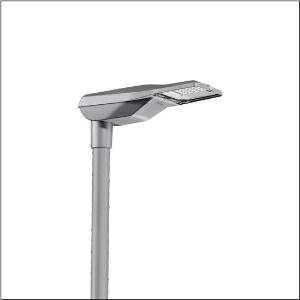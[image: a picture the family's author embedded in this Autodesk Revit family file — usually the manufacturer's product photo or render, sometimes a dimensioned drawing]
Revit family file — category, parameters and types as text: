
# Revit family: streetlight_sl_21_iq_micro___st1_5a_5xe1p41g08cb_60b9
name_source: partatom
category: Lighting Fixtures
units: mm (PartAtom-declared; Revit-internal decimal feet)

## family parameters
Cut with Voids When Loaded = No
Host = Face
Light Source = No
Part Type = Normal
Room Calculation Point = No
Round Connector Dimension = Use Diameter
Shared = No

## types (1)
- --- (1 x LED, 2930 lm, 19.4 W, 4000K)
    Apparent Load = 19 VA
    CIE Flux Codes = 22 53 95 100 100
    Color Rendering = 70
    Color Temperature = 4000K
    Default Elevation = 1800 mm
    Description = Streetlight SL 21 iQ micro, mast luminaire, primary light control with lens, of PMMA, primary optical cover: cover, of toughened safety glass, transparent, light distribution: ST1.5a, light emission: direct distribution, primary light characteristic: asymmetric, installation type: post-top, side-entry, LED, High Power LED, rated luminous flux: 2.930lm, luminous efficacy: 151lm/W, light colour: 740, colour temperature: 4000K, control: Street-Remote, Auto-Match, Temp-Guard, Lumen-Switch, Night-Set, Smart-Wire, Light-Fading, Desk-Remote (wireless, voltage-free reading and setting of iQ features in the workshop via application-optimized NFC function/RFID function), optimised constant luminous flux control (CLO 2.0), presetting dimming linear, mains connection: 220..240V, AC, 50/60Hz, start of lifetime: 19W, end of service life: 20W, reduction: 10W, luminaire housing, of diecast aluminium, powder-coated, Siteco® metallic grey (DB 702S), corrosivity category C5 mid according to DIN EN ISO 12944, please order mast flange separately, inclination adjustable: 0°, 5°, 10°, 15°, sealing non-destructively replaceable, multi-level sealing system, length: 528mm, width: 235mm, height: 110mm, mast flange for spigot size: 42mm (side-entry): 5XC10008XM4, 60/48mm (side-entry/post-top): 5XC10108XM2, 76/60mm (side-entry/post-top): 5XC10108XM1, protection rating (complete): IP66, insulation class (complete): insulation class II (safety insulation), certification: CE, ENEC, ENEC+, VDE, impact resistance: IK09, permissible operating ambient temperature for outdoor applications: -40..+50°C, standard-compliant lighting for roads and squares, packaging unit: 1 piece

Light Distribution: ST1.5a
    Height = 110 mm
    Lamp = 1 x LED
    Lamp Light Flux = 2930 lm
    Lamp Power = 19.4 W
    Lamp count = 1
    Length = 528 mm
    Luminous efficacy = 151 lm/W
    Manufacturer = Siteco
    ModVariant = No
    Model = 5XE1P41G08CB
    Number of Poles = 1
    OnlyDefault = Yes
    Power Factor = 1
    Product Name = Streetlight SL 21 iQ micro | ST1.5a
    Product group = mast luminaire | pylon top
    ProductGroupID = 6100
    Protection Class = Protection class II
    Protection Degree = IP 66
    RLX_Detail_Level = 1
    RLX_Emergency_Light_Flux = 0 lm
    RLX_Emergency_Type = 0
    RLX_Emergency_Type_DB = No
    RlxData = <blob elided: 102965 chars, md5=4679ed45>
    Socket = socket
    Standby Power = 0 W
    System Light Flux = 2930 lm
    System Power = 19 W
    Type Comments = factory setting: luminous flux: 100 % | dim-lin: 254 | 387 mA
    Type Image = l_1006881.jpg
    URL = http://relux.com
    VarID = @adj_087369
    Voltage = 0 V
    Weight = 0.00 kg
    Width = 235 mm

## geometry (parser evidence)
native form markers: Blend x4, Sweep x10
no freeform markers — native parametric forms only
